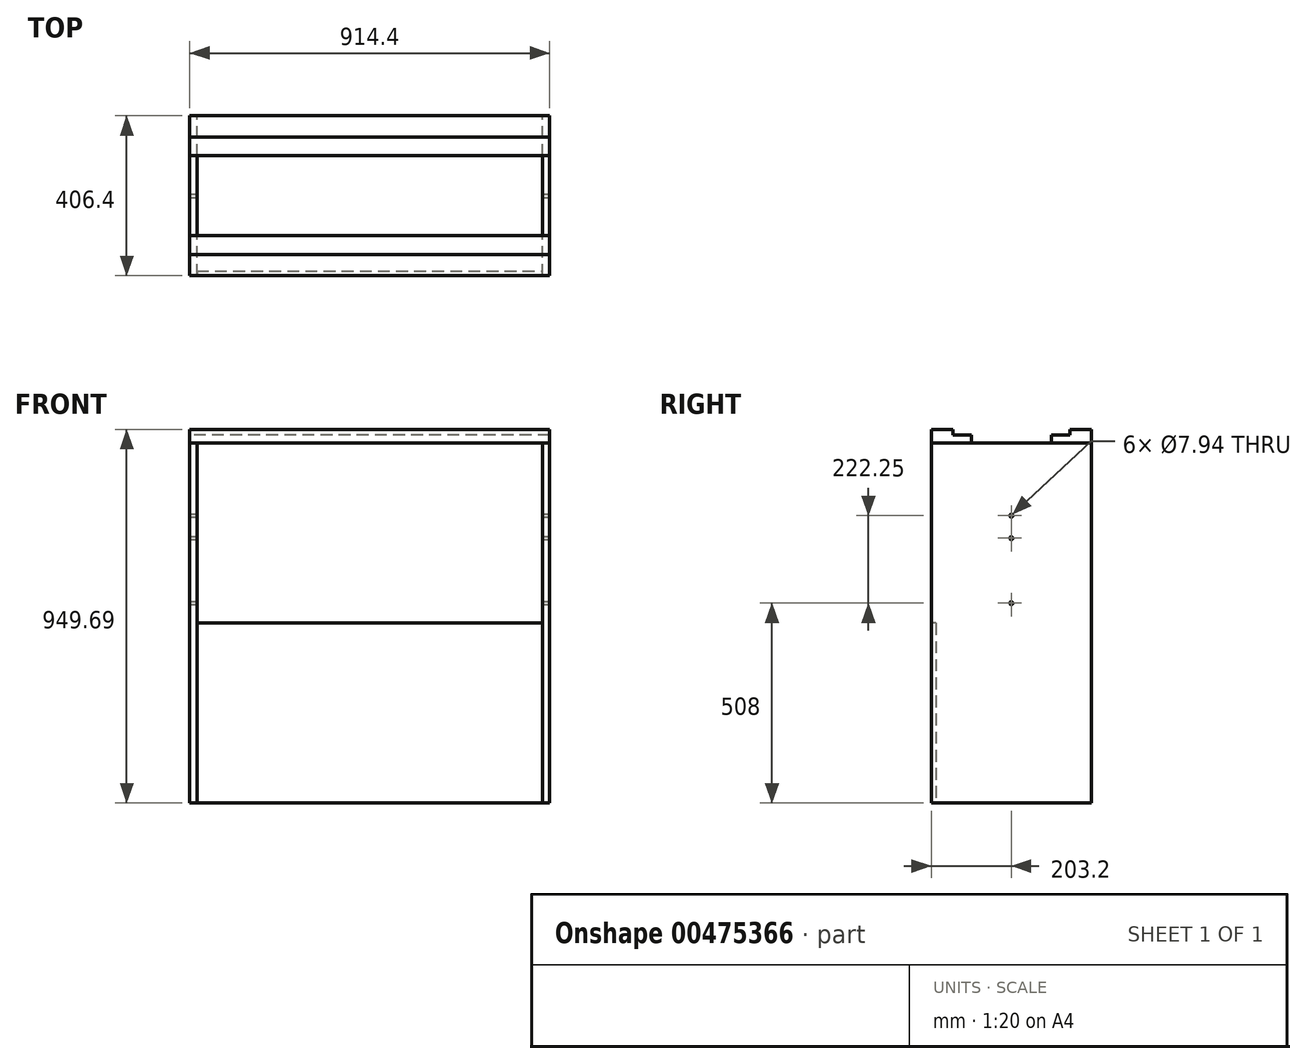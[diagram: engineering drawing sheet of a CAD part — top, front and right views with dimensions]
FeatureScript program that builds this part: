
annotation { "Feature Type Name" : "Feature", "Feature Type Description" : "" }
export const myFeature = defineFeature(function(context is Context, id is Id, definition is map)
    precondition{}
    {
        {
            var Q0;
            Q0=qCreatedBy(makeId("Right.planeOp"),FACE);
            var sketch = newSketch(context, id + "F0", { "sketchPlane" : qUnion([Q0])});
            skLineSegment(sketch, "E0.bottom", {"start": v(0, 0) * mm, "end": v(406.4, 0) * mm});
            skLineSegment(sketch, "E0.top", {"start": v(0, 914.4) * mm, "end": v(406.4, 914.4) * mm});
            skLineSegment(sketch, "E0.left", {"start": v(0, 0) * mm, "end": v(0, 914.4) * mm});
            skLineSegment(sketch, "E0.right", {"start": v(406.4, 0) * mm, "end": v(406.4, 914.4) * mm});
            skSolve(sketch);
        }
        {
            var Q0;
            Q0 = qSketchRegion(id + "F0", true);
            extrude(context, id + "F1", {"entities" : qUnion([Q0]), "depth" : 18 * mm});
        }
        {
            var Q0;
            Q0=qCreatedBy(makeId("Right.planeOp"),FACE);
            cPlane(context, id + "F2", {"entities" : qUnion([Q0]), "cplaneType" : CPlaneType.OFFSET, "offset" : 457.2 * mm, "width" : 152.4 * mm, "height" : 152.4 * mm});
        }
        {
            var Q0;
            Q0=makeQuery(id+"F1.opExtrude","SWEPT_BODY",BODY,{"disambiguationData":[OSD([sQuery(id+"F0.wireOp",EDGE,"E0.bottom"),sQuery(id+"F0.wireOp",EDGE,"E0.top"),sQuery(id+"F0.wireOp",EDGE,"E0.left"),sQuery(id+"F0.wireOp",EDGE,"E0.right")])]});
            var Q1;
            Q1=qCreatedBy(id+"F2.planeOp",FACE);
            mirror(context, id + "F3", {"operationType" : NewBodyOperationType.ADD, "entities" : qUnion([Q0]), "mirrorPlane" : qUnion([Q1])});
        }
        {
            var Q0;
            Q0=makeQuery(id+"F3.opPattern","COPY",FACE,{"derivedFrom":makeQuery(id+"F1.opExtrude","CAP_FACE",FACE,{"disambiguationData":[OSD([sQuery(id+"F0.wireOp",EDGE,"E0.bottom"),sQuery(id+"F0.wireOp",EDGE,"E0.top"),sQuery(id+"F0.wireOp",EDGE,"E0.left"),sQuery(id+"F0.wireOp",EDGE,"E0.right")])],"isStart":false}),"instanceName":"1"});
            var sketch = newSketch(context, id + "F4", { "sketchPlane" : qUnion([Q0])});
            skLineSegment(sketch, "E1", {"start": v(-203.2, 914.4) * mm, "end": v(-203.2, 0) * mm, "construction": true});
            skCircle(sketch, "E2", {"center": v(-203.2, 730.25) * mm, "radius": 3.97 * mm});
            skCircle(sketch, "E3", {"center": v(-203.2, 673.1) * mm, "radius": 3.97 * mm});
            skCircle(sketch, "E4", {"center": v(-203.2, 508) * mm, "radius": 3.97 * mm});
            skSolve(sketch);
        }
        {
            var Q0;
            Q0 = qSketchRegion(id + "F4", true);
            extrude(context, id + "F5", {"entities" : qUnion([Q0]), "operationType" : NewBodyOperationType.REMOVE, "endBound" : BoundingType.SYMMETRIC, "depth" : 2032 * mm});
        }
        {
            var Q0;
            Q0=makeQuery(id+"F1.opExtrude","CAP_FACE",FACE,{"disambiguationData":[OSD([sQuery(id+"F0.wireOp",EDGE,"E0.bottom"),sQuery(id+"F0.wireOp",EDGE,"E0.top"),sQuery(id+"F0.wireOp",EDGE,"E0.left"),sQuery(id+"F0.wireOp",EDGE,"E0.right")])],"isStart":true});
            var sketch = newSketch(context, id + "F6", { "sketchPlane" : qUnion([Q0])});
            skLineSegment(sketch, "E5.0", {"start": v(0, 914.4) * mm, "end": v(-101.6, 914.4) * mm});
            skLineSegment(sketch, "E6", {"start": v(-203.2, 914.4) * mm, "end": v(-203.2, 975.24) * mm, "construction": true});
            skPoint(sketch, "E6.endSnap0", {"position": v(-203.2, 914.4) * mm});
            skLineSegment(sketch, "E7.bottom", {"start": v(-406.4, 914.4) * mm, "end": v(-304.8, 914.4) * mm});
            skLineSegment(sketch, "E7.top", {"start": v(-406.4, 949.7) * mm, "end": v(-352.02, 949.7) * mm});
            skLineSegment(sketch, "E7.left", {"start": v(-406.4, 914.4) * mm, "end": v(-406.4, 949.7) * mm});
            skLineSegment(sketch, "E7.right", {"start": v(-304.8, 914.4) * mm, "end": v(-304.8, 935.25) * mm});
            skLineSegment(sketch, "E8", {"start": v(-352.02, 949.7) * mm, "end": v(-352.02, 935.25) * mm});
            skLineSegment(sketch, "E9", {"start": v(-352.02, 935.25) * mm, "end": v(-304.8, 935.25) * mm});
            skLineSegment(sketch, "E10.MirrorCS", {"start": v(0, 914.4) * mm, "end": v(0, 949.7) * mm});
            skLineSegment(sketch, "E11.MirrorCS", {"start": v(0, 949.7) * mm, "end": v(-54.38, 949.7) * mm});
            skLineSegment(sketch, "E12.MirrorCS", {"start": v(-54.38, 949.7) * mm, "end": v(-54.38, 935.25) * mm});
            skLineSegment(sketch, "E13.MirrorCS", {"start": v(-54.38, 935.25) * mm, "end": v(-101.6, 935.25) * mm});
            skLineSegment(sketch, "E14.MirrorCS", {"start": v(-101.6, 914.4) * mm, "end": v(-101.6, 935.25) * mm});
            skLineSegment(sketch, "E15.trimOffspring", {"start": v(-304.8, 914.4) * mm, "end": v(-406.4, 914.4) * mm});
            skSolve(sketch);
        }
        {
            var Q0;
            Q0 = qSketchRegion(id + "F6", true);
            var Q1;
            Q1=makeQuery(id+"F3.opPattern","COPY",FACE,{"derivedFrom":makeQuery(id+"F1.opExtrude","CAP_FACE",FACE,{"disambiguationData":[OSD([sQuery(id+"F0.wireOp",EDGE,"E0.bottom"),sQuery(id+"F0.wireOp",EDGE,"E0.top"),sQuery(id+"F0.wireOp",EDGE,"E0.left"),sQuery(id+"F0.wireOp",EDGE,"E0.right")])],"isStart":true}),"instanceName":"1"});
            extrude(context, id + "F7", {"entities" : qUnion([Q0]), "endBound" : BoundingType.UP_TO_SURFACE, "oppositeDirection" : true, "endBoundEntityFace" : qUnion([Q1]), "depth" : 25.4 * mm});
        }
        {
            var Q0;
            Q0=makeQuery(id+"F3.opPattern","COPY",FACE,{"derivedFrom":makeQuery(id+"F1.opExtrude","CAP_FACE",FACE,{"disambiguationData":[OSD([sQuery(id+"F0.wireOp",EDGE,"E0.bottom"),sQuery(id+"F0.wireOp",EDGE,"E0.top"),sQuery(id+"F0.wireOp",EDGE,"E0.left"),sQuery(id+"F0.wireOp",EDGE,"E0.right")])],"isStart":false}),"instanceName":"1"});
            var sketch = newSketch(context, id + "F8", { "sketchPlane" : qUnion([Q0])});
            skLineSegment(sketch, "E16.bottom", {"start": v(0, 0) * mm, "end": v(-12, 0) * mm});
            skLineSegment(sketch, "E16.top", {"start": v(0, 457.2) * mm, "end": v(-12, 457.2) * mm});
            skLineSegment(sketch, "E16.left", {"start": v(0, 0) * mm, "end": v(0, 457.2) * mm});
            skLineSegment(sketch, "E16.right", {"start": v(-12, 0) * mm, "end": v(-12, 457.2) * mm});
            skSolve(sketch);
        }
        {
            var Q0;
            Q0 = qSketchRegion(id + "F8", true);
            extrude(context, id + "F9", {"entities" : qUnion([Q0]), "endBound" : BoundingType.UP_TO_NEXT, "depth" : 25.4 * mm});
        }
    });
